# Revit family: Hager-Orion_Plus-IP65-D300-Cl.II-Poly_double_encl-630A-Floor_installation-NoHosted-CH-en
name_source: partatom
category: Electrical Equipment
units: mm (PartAtom-declared; Revit-internal decimal feet)

## family parameters
Always vertical = Yes
Cut with Voids When Loaded = No
Panel Configuration = Two Columns, Circuits Across
Part Type = Panelboard
Room Calculation Point = No
Round Connector Dimension = Use Diameter
Shared = No
Work Plane-Based = Yes

## types (15) — shared parameters
Default Elevation = 1219 mm
EF000003 - Mounting method = EV012274 - Floor installation
EF000007 - Colour = EV000270 - Grey
EF000049 - Depth = 300 mm  [stored 0.984252 ft]
EF000116 - RAL-number = 7035
EF001131 - Internal depth = 300 mm  [stored 0.984252 ft]
EF001596 - Material housing = EV000139 - Plastic
EF001613 - Circuit integrity = EV000494 - None
EF005474 - Degree of protection (IP) = EV006421 - IP65
EF006306 - With lock = Yes
EF007800 - Suitable for lightning protection = No
EF008873 - Nominal current (In) = 630 A
EF009170 - Material plate thickness cabinet = 2 mm  [stored 0.00656168 ft]
EF009171 - Material plate thickness door/cover = 2 mm  [stored 0.00656168 ft]
EF015940 - Cover with overpressure release = No
HG000003 - Range = Orion Plus
HG000006 - Flush mounted = No
HG000010 - Asymmetric doors = No
HG000023 - Double section enclosure = Yes
HG000024 - Bottom section height = 600 mm
HG000026 - Floor standing = Yes
HG000027 - Plinth height = 70 mm  [stored 0.229659 ft]
Manufacturer = Hager
Type Comments = Orion Plus
zero-valued in all types: EF000218 - Built-in depth, EF000437 - Number of conduit inlets, EF009554 - Number of openings for flange plates

## per-type parameters (varying)
| type | EF000008 - Width | EF000040 - Height | EF000118 - With mounting plate | EF000266 - Number of rows | EF000339 - Type of cover | EF001088 - Extension possible | EF002950 - Width in number of modular spacings | EF003532 - Suitable for outdoor use | EF004293 - Impact strength | EF004427 - Number of modules | EF004464 - Type of door | EF006244 - Transparent cover/door | EF009212 - Cover model | HG000002 - With door or cover | HG000004 - Manufacturer reference | HG000009 - Double swing door |
| Floor installation IP65 W1100 H1150 D300  - FL360B | 1100 mm | 1150 mm | No | 3 | EV004216 - Door | Yes | 0 | Yes | EV008784 - IK10 | 138 | EV002646 - Single | Yes | EV009916 - With notch | Yes | FL360B | Yes |
| Floor installation IP65 W1100 H1450 D300  - FL362B | 1100 mm | 1450 mm  [stored 4.75722 ft] | No | 3 | EV004216 - Door | Yes | 0 | Yes | EV008784 - IK10 | 138 | EV002646 - Single | Yes | EV009916 - With notch | Yes | FL362B | Yes |
| Floor installation IP65 W1100 H1750 D300  - FL364B | 1100 mm | 1750 mm  [stored 5.74147 ft] | No | 3 | EV004216 - Door | Yes | 0 | Yes | EV008784 - IK10 | 138 | EV002646 - Single | Yes | EV009916 - With notch | Yes | FL364B | Yes |
| Floor installation IP65 W1100 H1750 D300  - FL366B | 1100 mm | 1750 mm  [stored 5.74147 ft] | No | 5 | EV004216 - Door | Yes | 0 | Yes | EV008784 - IK10 | 230 | EV002646 - Single | Yes | EV009916 - With notch | Yes | FL366B | Yes |
| Floor installation IP65 W1100 H2050 D300  - FL368B | 1100 mm | 2050 mm  [stored 6.72572 ft] | Yes | 5 | EV001012 - Cover | No | 0 | No | EV006814 - IK08 | 230 | EV002646 - Single | No | EV000116 - Closed | Yes | FL368B | Yes |
| Floor installation IP65 W600 H1150 D300  - FL340B | 600 mm | 1150 mm | No | 3 | EV004216 - Door | Yes | 0 | Yes | EV008784 - IK10 | 69 | EV002646 - Single | Yes | EV009916 - With notch | Yes | FL340B | No |
| Floor installation IP65 W600 H1450 D300  - FL342B | 600 mm | 1450 mm  [stored 4.75722 ft] | No | 3 | EV004216 - Door | Yes | 0 | Yes | EV008784 - IK10 | 69 | EV002646 - Single | Yes | EV009916 - With notch | No | FL342B | No |
| Floor installation IP65 W600 H1750 D300  - FL344B | 600 mm | 1750 mm  [stored 5.74147 ft] | No | 9 | EV004216 - Door | Yes | 23 | No |  | 0 |  | Yes | EV009916 - With notch | Yes | FL344B | No |
| Floor installation IP65 W600 H1750 D300  - FL346B | 600 mm | 1750 mm  [stored 5.74147 ft] | No | 5 | EV004216 - Door | Yes | 0 | Yes | EV008784 - IK10 | 115 | EV002646 - Single | Yes | EV009916 - With notch | Yes | FL346B | No |
| Floor installation IP65 W600 H2050 D300  - FL348B | 600 mm | 2050 mm  [stored 6.72572 ft] | No | 3 | EV004216 - Door | Yes | 0 | Yes | EV008784 - IK10 | 115 | EV002646 - Single | Yes | EV009916 - With notch | Yes | FL348B | No |
| Floor installation IP65 W850 H1150 D300  - FL350B | 850 mm  [stored 2.78871 ft] | 1150 mm | No | 3 | EV004216 - Door | Yes | 0 | Yes | EV008784 - IK10 | 111 | EV002646 - Single | Yes | EV009916 - With notch | Yes | FL350B | No |
| Floor installation IP65 W850 H1450 D300  - FL352B | 850 mm  [stored 2.78871 ft] | 1450 mm  [stored 4.75722 ft] | Yes | 3 | EV001012 - Cover | No | 0 | No | EV006814 - IK08 | 111 | EV002646 - Single | No | EV000116 - Closed | Yes | FL352B | No |
| Floor installation IP65 W850 H1750 D300  - FL354B | 850 mm  [stored 2.78871 ft] | 1750 mm  [stored 5.74147 ft] | Yes | 3 | EV001012 - Cover | No | 0 | No | EV006814 - IK08 | 111 | EV002646 - Single | No | EV000116 - Closed | Yes | FL354B | No |
| Floor installation IP65 W850 H1750 D300  - FL356B | 850 mm  [stored 2.78871 ft] | 1750 mm  [stored 5.74147 ft] | No | 5 | EV004216 - Door | Yes | 0 | Yes | EV008784 - IK10 | 185 | EV002646 - Single | Yes | EV009916 - With notch | Yes | FL356B | No |
| Floor installation IP65 W850 H2050 D300  - FL358B | 850 mm  [stored 2.78871 ft] | 2050 mm  [stored 6.72572 ft] | No | 5 | EV004216 - Door | Yes | 0 | Yes | EV008784 - IK10 | 185 | EV002646 - Single | Yes | EV009916 - With notch | Yes | FL358B | No |

note: [stored X ft] marks values corroborated as IEEE doubles in the binary element streams (Revit-internal decimal feet)

## geometry (parser evidence)
native form markers: Blend x4, Sweep x5
no freeform markers — native parametric forms only
